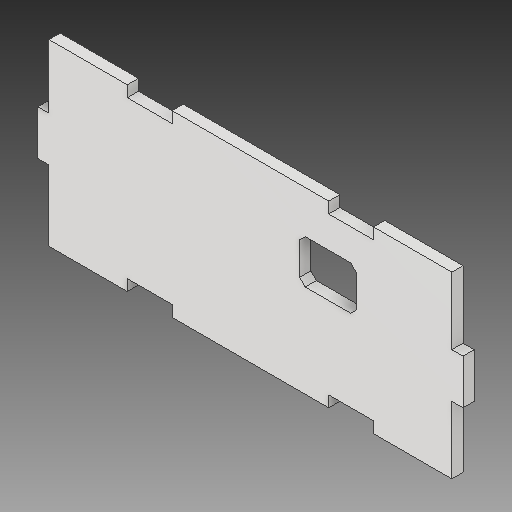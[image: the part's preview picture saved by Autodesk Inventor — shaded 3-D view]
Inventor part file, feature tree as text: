
AUTODESK INVENTOR PART (.ipt)
format: ipt  version: 2018.2 (Build 222227000, 227)  size: 129,536 bytes
history: native  units: in
note: dims shown in document units (in); Inventor stores cm internally (conversion verified against a paired STEP export)
features: reference x10, other x3, extrude x1, sketch x1
ambient origin geometry x8: Origin, YZ Plane, XZ Plane, XY Plane, X Axis, Y Axis, Z Axis, Center Point
bodies: Solid1 (feature_tree)
feature tree (15):
  extrude  "Extrusion1"  Depth=0.25in
  sketch  "Sketch1"  dims[d0=0.125in d1=0.0in d2=0.25in d3=0.5in d4=0.25in d5=0.5in]
  reference  "Reference2"
  reference  "Reference3"
  reference  "Reference4"
  reference  "Reference5"
  reference  "Reference6"
  reference  "Reference7"
  reference  "Reference8"
  reference  "Reference9"
  reference  "Reference10"
  reference  "Reference11"
  other  "Assembly1.iam"
  other  "Part64:1"
  other  "Face:1"
